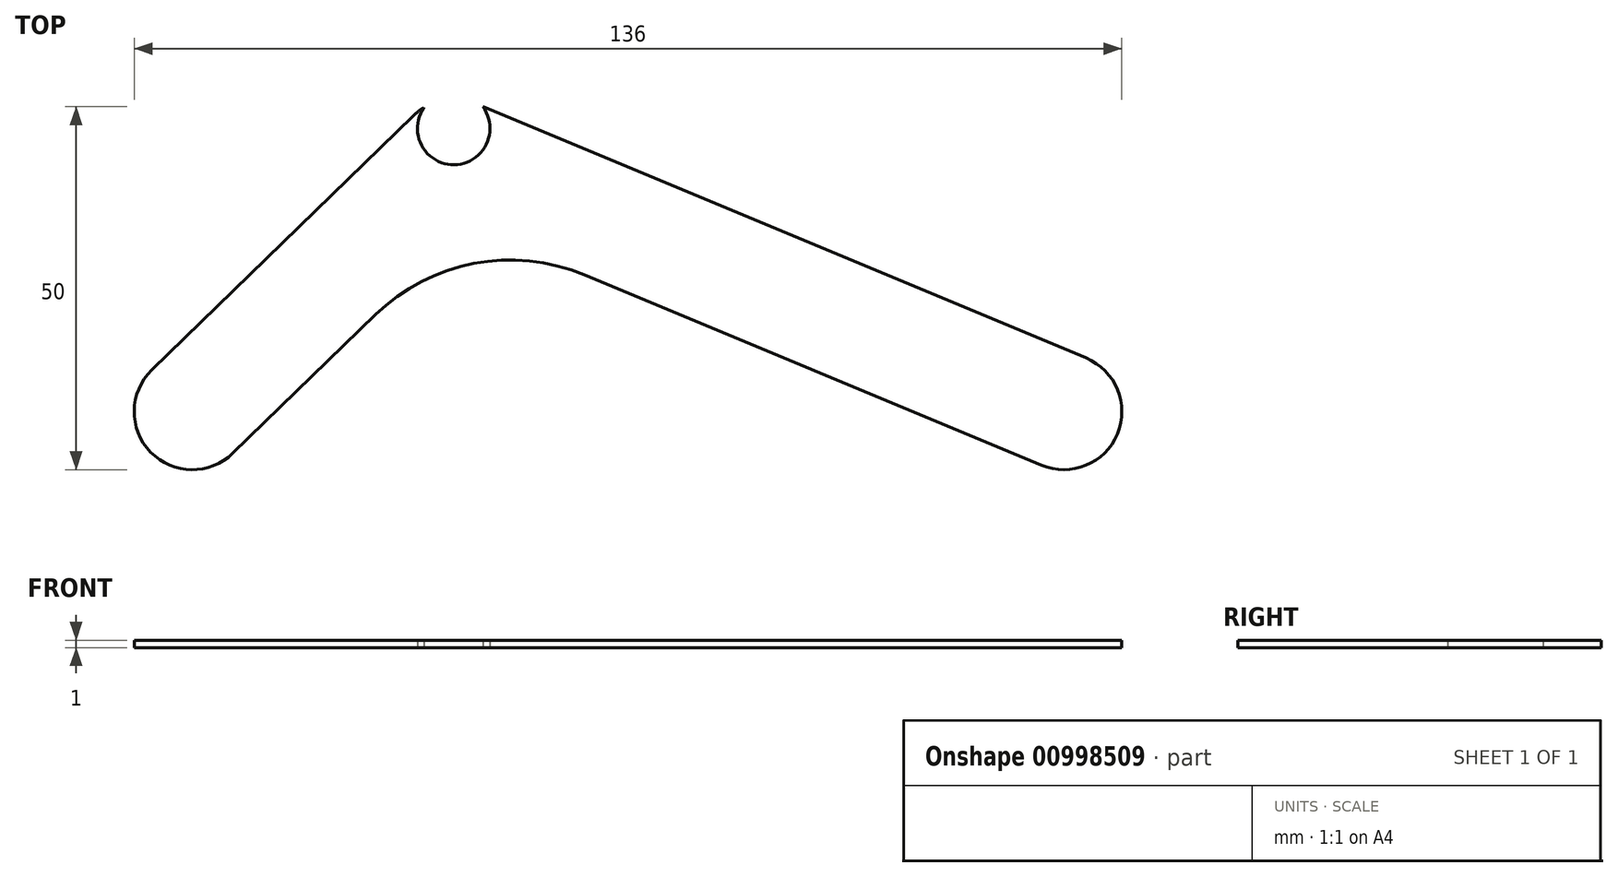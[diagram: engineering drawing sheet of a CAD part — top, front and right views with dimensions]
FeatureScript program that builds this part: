
annotation { "Feature Type Name" : "Feature", "Feature Type Description" : "" }
export const myFeature = defineFeature(function(context is Context, id is Id, definition is map)
    precondition{}
    {
        {
            var Q0;
            Q0=qCreatedBy(makeId("Top.planeOp"),FACE);
            var sketch = newSketch(context, id + "F0", { "sketchPlane" : qUnion([Q0])});
            skCircle(sketch, "E0", {"center": v(0, 35) * mm, "radius": 8 * mm});
            skCircle(sketch, "E1", {"center": v(84, 0) * mm, "radius": 8 * mm});
            skCircle(sketch, "E2", {"center": v(-36, 0) * mm, "radius": 8 * mm});
            skLineSegment(sketch, "E3", {"start": v(80.92, -7.38) * mm, "end": v(-3.08, 27.62) * mm});
            skLineSegment(sketch, "E4", {"start": v(-5.58, 40.74) * mm, "end": v(-41.58, 5.74) * mm});
            skLineSegment(sketch, "E5", {"start": v(-30.42, -5.74) * mm, "end": v(5.58, 29.26) * mm});
            skLineSegment(sketch, "E6", {"start": v(87.08, 7.38) * mm, "end": v(3.08, 42.38) * mm});
            skCircle(sketch, "E7", {"center": v(0, 39) * mm, "radius": 5 * mm});
            skSolve(sketch);
        }
        {
            var Q0;
            {var subQ0=sQuery(id+"F0.wireOp",EDGE,"E4");Q0=makeQuery(id+"F0.imprint","IMPRINT",FACE,{"disambiguationData":[TD([[makeQuery(id+"F0.imprint","IMPRINT",EDGE,{"derivedFrom":subQ0}),1.0]])]});}
            var Q1;
            {var subQ0=sQuery(id+"F0.wireOp",EDGE,"E2");var subQ1=makeQuery(id+"F0.imprint","INTERSECT",VERTEX,{"derivedFrom":[subQ0,sQuery(id+"F0.wireOp",EDGE,"E4")]});Q1=makeQuery(id+"F0.imprint","IMPRINT",FACE,{"disambiguationData":[TD([[makeQuery(id+"F0.imprint","IMPRINT",EDGE,{"disambiguationData":[TD([[subQ1,-1.0]])],"derivedFrom":subQ0}),1.0]])]});}
            var Q2;
            {var subQ0=sQuery(id+"F0.wireOp",EDGE,"E1");var subQ1=makeQuery(id+"F0.imprint","INTERSECT",VERTEX,{"derivedFrom":[subQ0,sQuery(id+"F0.wireOp",EDGE,"E3")]});Q2=makeQuery(id+"F0.imprint","IMPRINT",FACE,{"disambiguationData":[TD([[makeQuery(id+"F0.imprint","IMPRINT",EDGE,{"disambiguationData":[TD([[subQ1,1.0]])],"derivedFrom":subQ0}),1.0]])]});}
            var Q3;
            {var subQ0=sQuery(id+"F0.wireOp",EDGE,"E5");var subQ1=sQuery(id+"F0.wireOp",EDGE,"E0");var subQ2=makeQuery(id+"F0.imprint","INTERSECT",VERTEX,{"derivedFrom":[subQ1,subQ0]});Q3=makeQuery(id+"F0.imprint","IMPRINT",FACE,{"disambiguationData":[TD([[makeQuery(id+"F0.imprint","IMPRINT",EDGE,{"disambiguationData":[TD([[subQ2,-1.0]])],"derivedFrom":subQ1}),-1.0]])]});}
            var Q4;
            {var subQ0=sQuery(id+"F0.wireOp",EDGE,"E0");var subQ1=makeQuery(id+"F0.imprint","INTERSECT",VERTEX,{"derivedFrom":[subQ0,sQuery(id+"F0.wireOp",EDGE,"E3")]});Q4=makeQuery(id+"F0.imprint","IMPRINT",FACE,{"disambiguationData":[TD([[makeQuery(id+"F0.imprint","IMPRINT",EDGE,{"disambiguationData":[TD([[subQ1,1.0]])],"derivedFrom":subQ0}),1.0]])]});}
            var Q5;
            {var subQ0=sQuery(id+"F0.wireOp",EDGE,"E3");var subQ1=sQuery(id+"F0.wireOp",EDGE,"E0");var subQ2=makeQuery(id+"F0.imprint","INTERSECT",VERTEX,{"derivedFrom":[subQ1,subQ0]});Q5=makeQuery(id+"F0.imprint","IMPRINT",FACE,{"disambiguationData":[TD([[makeQuery(id+"F0.imprint","IMPRINT",EDGE,{"disambiguationData":[TD([[subQ2,1.0]])],"derivedFrom":subQ1}),-1.0]])]});}
            var Q6;
            {var subQ0=sQuery(id+"F0.wireOp",EDGE,"E3");var subQ1=sQuery(id+"F0.wireOp",EDGE,"E0");var subQ2=makeQuery(id+"F0.imprint","INTERSECT",VERTEX,{"derivedFrom":[subQ1,subQ0]});Q6=makeQuery(id+"F0.imprint","IMPRINT",FACE,{"disambiguationData":[TD([[makeQuery(id+"F0.imprint","IMPRINT",EDGE,{"disambiguationData":[TD([[subQ2,-1.0]])],"derivedFrom":subQ1}),-1.0]])]});}
            extrude(context, id + "F1", {"entities" : qUnion([Q0, Q1, Q2, Q3, Q4, Q5, Q6]), "depth" : 1 * mm, "offsetDistance" : 25 * mm});
        }
        {
            var Q0;
            Q0=makeQuery(id+"F1.opExtrude","SWEPT_EDGE",EDGE,{"disambiguationData":[OSD([sQuery(id+"F0.wireOp",EDGE,"E3"),sQuery(id+"F0.wireOp",EDGE,"E5")])]});
            fillet(context, id + "F2", {"entities" : qUnion([Q0]), "radius" : 26.62 * mm, "tangentPropagation" : true, "allowEdgeOverflow" : false});
        }
    });
